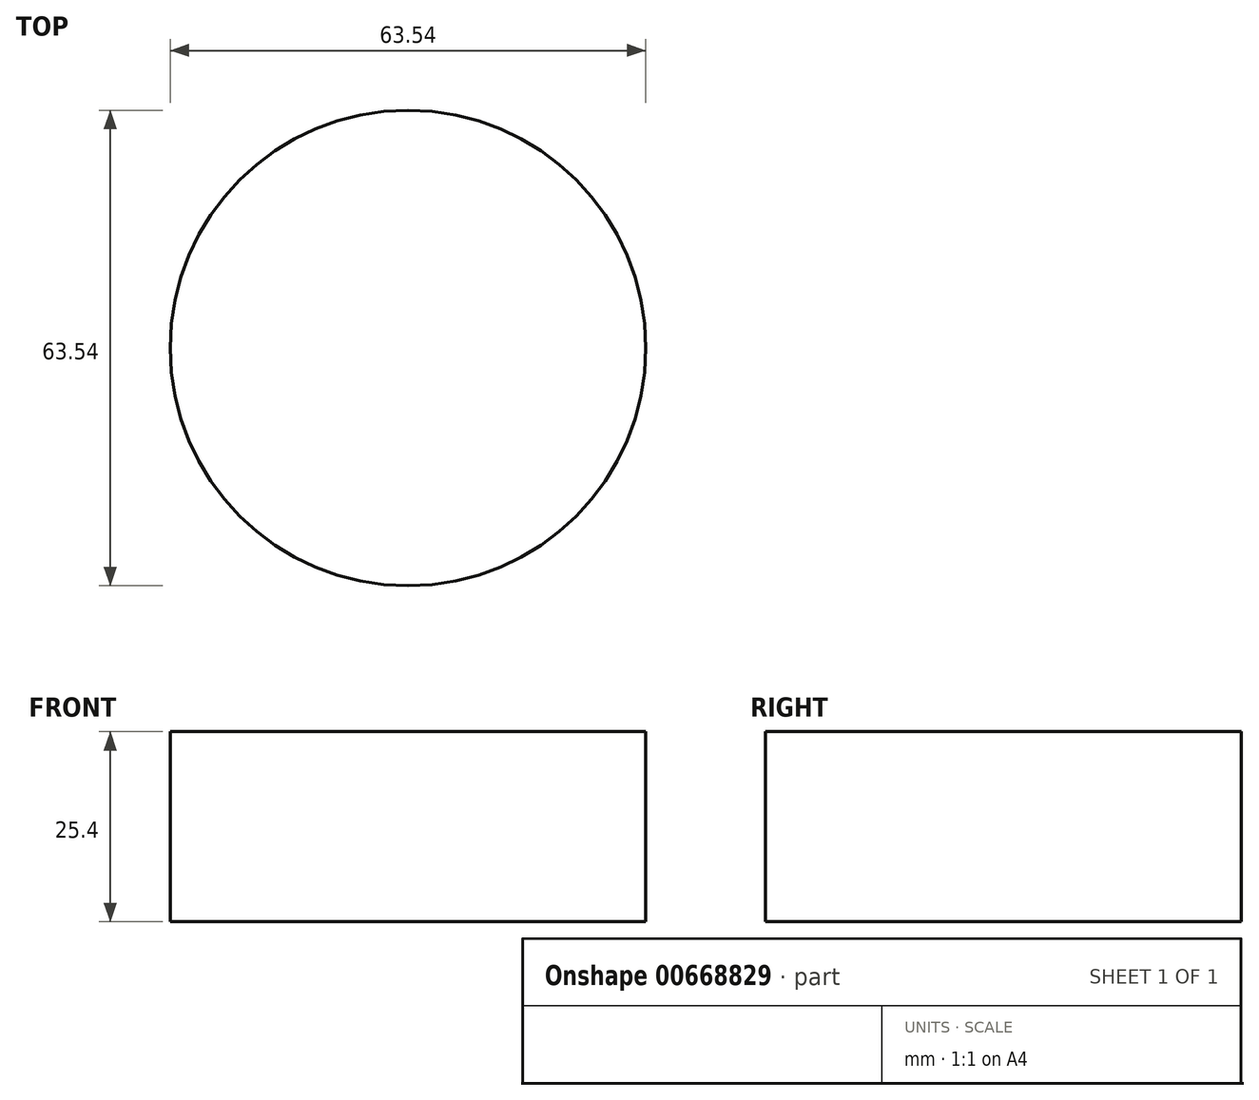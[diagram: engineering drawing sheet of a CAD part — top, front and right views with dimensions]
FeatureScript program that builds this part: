
annotation { "Feature Type Name" : "Feature", "Feature Type Description" : "" }
export const myFeature = defineFeature(function(context is Context, id is Id, definition is map)
    precondition{}
    {
        {
            var Q0;
            Q0=qCreatedBy(makeId("Top.planeOp"),FACE);
            var sketch = newSketch(context, id + "F0", { "sketchPlane" : qUnion([Q0])});
            skCircle(sketch, "E0", {"center": v(0, 0) * mm, "radius": 31.77 * mm});
            skSolve(sketch);
        }
        {
            var Q0;
            Q0=makeQuery(id+"F0.imprint","IMPRINT",FACE,{"disambiguationData":[TD([[makeQuery(id+"F0.imprint","IMPRINT",EDGE,{"derivedFrom":sQuery(id+"F0.wireOp",EDGE,"E0")}),1.0]])]});
            extrude(context, id + "F1", {"entities" : qUnion([Q0]), "depth" : 25.4 * mm, "offsetDistance" : 25.4 * mm});
        }
    });
